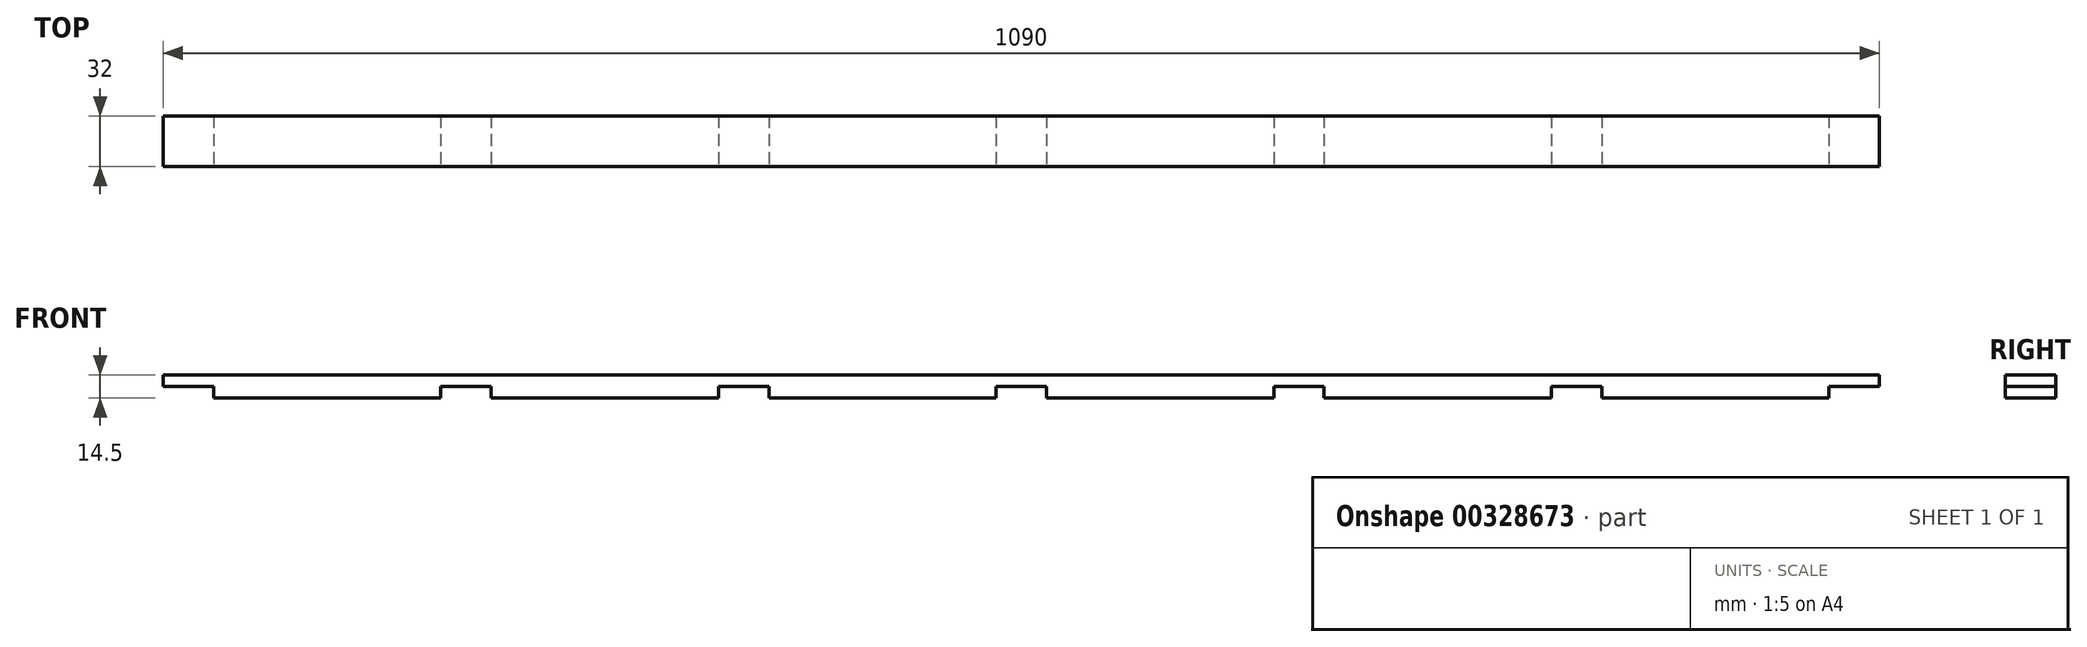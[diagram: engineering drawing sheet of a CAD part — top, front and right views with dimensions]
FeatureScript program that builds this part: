
annotation { "Feature Type Name" : "Feature", "Feature Type Description" : "" }
export const myFeature = defineFeature(function(context is Context, id is Id, definition is map)
    precondition{}
    {
        {
            var Q0;
            Q0=qCreatedBy(makeId("Front.planeOp"),FACE);
            var sketch = newSketch(context, id + "F0", { "sketchPlane" : qUnion([Q0])});
            skLineSegment(sketch, "E0.bottom", {"start": v(0, 0) * mm, "end": v(-1090, 0) * mm});
            skLineSegment(sketch, "E0.top", {"start": v(-32, -14.5) * mm, "end": v(-176.3, -14.5) * mm});
            skLineSegment(sketch, "E0.left", {"start": v(0, 0) * mm, "end": v(0, -7.25) * mm});
            skLineSegment(sketch, "E0.right", {"start": v(-1090, 0) * mm, "end": v(-1090, -7.25) * mm});
            skLineSegment(sketch, "E1", {"start": v(0, -7.25) * mm, "end": v(-32, -7.25) * mm});
            skPoint(sketch, "E1.endSnap0", {"position": v(0, -7.25) * mm});
            skLineSegment(sketch, "E2", {"start": v(-32, -7.25) * mm, "end": v(-32, -14.5) * mm});
            skPoint(sketch, "E3.orphan", {"position": v(0, -14.5) * mm});
            skLineSegment(sketch, "E4", {"start": v(-208.3, -14.5) * mm, "end": v(-208.3, -7.25) * mm});
            skLineSegment(sketch, "E5", {"start": v(-176.3, -7.25) * mm, "end": v(-208.3, -7.25) * mm});
            skLineSegment(sketch, "E6", {"start": v(-176.3, -7.25) * mm, "end": v(-176.3, -14.5) * mm});
            skLineSegment(sketch, "E7", {"start": v(-352.7, -14.5) * mm, "end": v(-352.7, -7.25) * mm});
            skLineSegment(sketch, "E8", {"start": v(-352.7, -7.25) * mm, "end": v(-384.7, -7.25) * mm});
            skLineSegment(sketch, "E9", {"start": v(-384.7, -7.25) * mm, "end": v(-384.7, -14.5) * mm});
            skLineSegment(sketch, "E10", {"start": v(-561, -14.5) * mm, "end": v(-561, -7.25) * mm});
            skLineSegment(sketch, "E11", {"start": v(-529, -7.25) * mm, "end": v(-561, -7.25) * mm});
            skLineSegment(sketch, "E12", {"start": v(-529, -7.25) * mm, "end": v(-529, -14.5) * mm});
            skLineSegment(sketch, "E13", {"start": v(-705.3, -14.5) * mm, "end": v(-705.3, -7.25) * mm});
            skLineSegment(sketch, "E14", {"start": v(-705.3, -7.25) * mm, "end": v(-737.3, -7.25) * mm});
            skLineSegment(sketch, "E15", {"start": v(-737.3, -7.25) * mm, "end": v(-737.3, -14.5) * mm});
            skLineSegment(sketch, "E16", {"start": v(-913.7, -14.5) * mm, "end": v(-913.7, -7.25) * mm});
            skLineSegment(sketch, "E17", {"start": v(-881.7, -7.25) * mm, "end": v(-913.7, -7.25) * mm});
            skLineSegment(sketch, "E18", {"start": v(-881.7, -7.25) * mm, "end": v(-881.7, -14.5) * mm});
            skLineSegment(sketch, "E19.trimOffspring", {"start": v(-913.7, -14.5) * mm, "end": v(-1058, -14.5) * mm});
            skLineSegment(sketch, "E20.trimOffspring", {"start": v(-737.3, -14.5) * mm, "end": v(-881.7, -14.5) * mm});
            skLineSegment(sketch, "E21.trimOffspring", {"start": v(-561, -14.5) * mm, "end": v(-705.3, -14.5) * mm});
            skLineSegment(sketch, "E22.trimOffspring", {"start": v(-208.3, -14.5) * mm, "end": v(-352.7, -14.5) * mm});
            skLineSegment(sketch, "E23.trimOffspring", {"start": v(-384.7, -14.5) * mm, "end": v(-529, -14.5) * mm});
            skLineSegment(sketch, "E24", {"start": v(-1090, -7.25) * mm, "end": v(-1058, -7.25) * mm});
            skLineSegment(sketch, "E25", {"start": v(-1058, -7.25) * mm, "end": v(-1058, -14.5) * mm});
            skPoint(sketch, "E26.orphan", {"position": v(-1090, -14.5) * mm});
            skSolve(sketch);
        }
        {
            var Q0;
            Q0=makeQuery(id+"F0.imprint","IMPRINT",FACE,{"disambiguationData":[TD([[makeQuery(id+"F0.imprint","IMPRINT",EDGE,{"derivedFrom":sQuery(id+"F0.wireOp",EDGE,"E0.bottom")}),1.0]])]});
            extrude(context, id + "F1", {"entities" : qUnion([Q0]), "oppositeDirection" : true, "depth" : 32 * mm});
        }
    });
